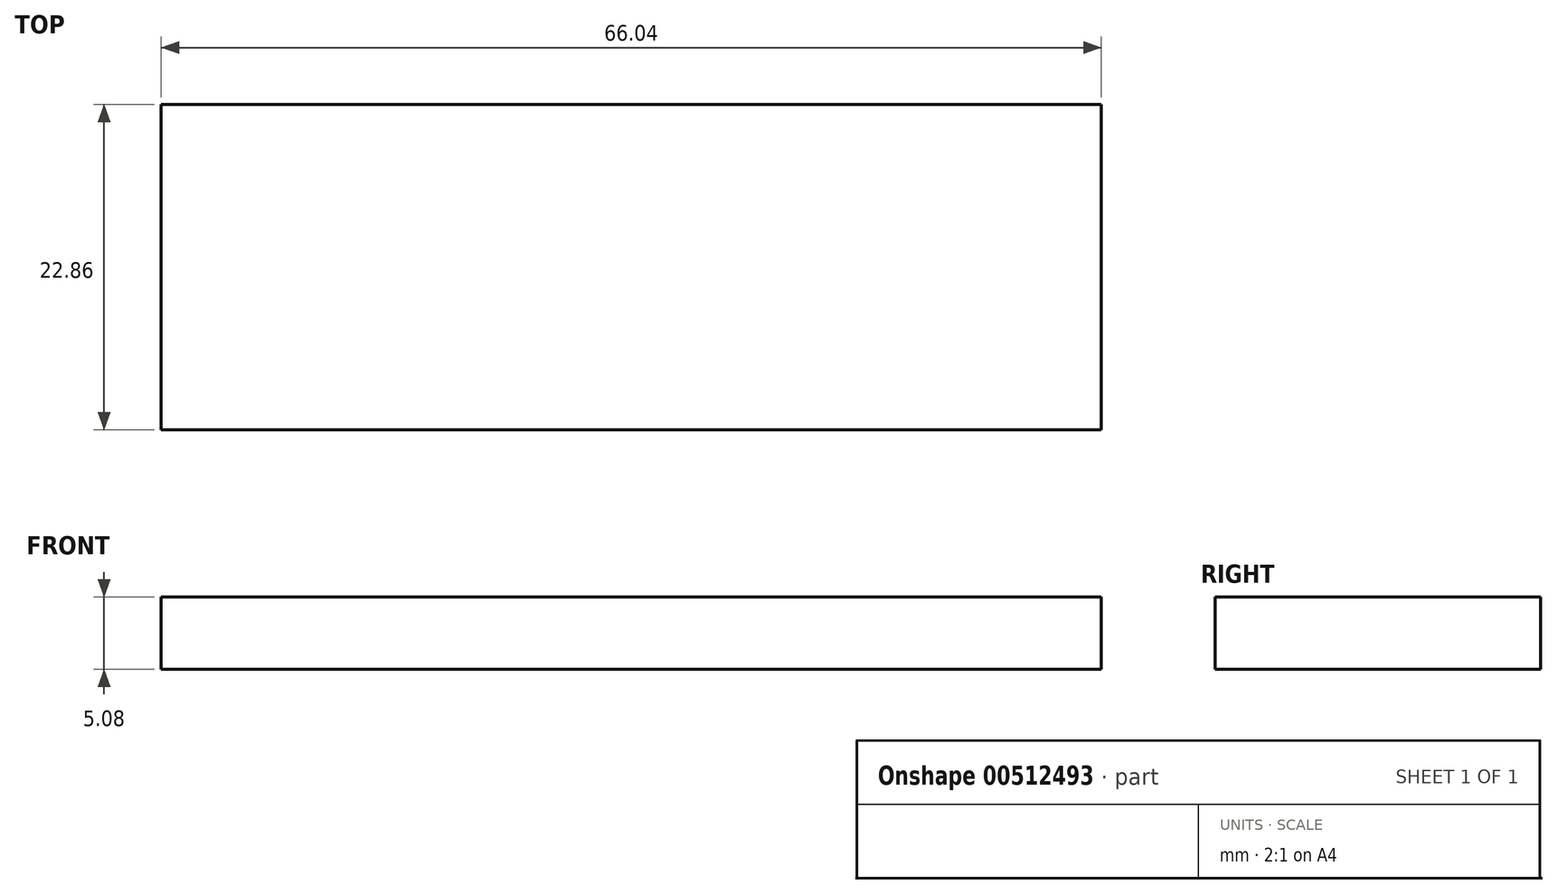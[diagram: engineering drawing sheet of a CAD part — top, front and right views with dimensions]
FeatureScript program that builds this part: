
annotation { "Feature Type Name" : "Feature", "Feature Type Description" : "" }
export const myFeature = defineFeature(function(context is Context, id is Id, definition is map)
    precondition{}
    {
        {
            var Q0;
            Q0=qCreatedBy(makeId("Top.planeOp"),FACE);
            var sketch = newSketch(context, id + "F0", { "sketchPlane" : qUnion([Q0])});
            skLineSegment(sketch, "E0.bottom", {"start": v(-80, 30.94) * mm, "end": v(-13.97, 30.94) * mm});
            skLineSegment(sketch, "E0.top", {"start": v(-80, 8.08) * mm, "end": v(-13.97, 8.08) * mm});
            skLineSegment(sketch, "E0.left", {"start": v(-80, 30.94) * mm, "end": v(-80, 8.08) * mm});
            skLineSegment(sketch, "E0.right", {"start": v(-13.97, 30.94) * mm, "end": v(-13.97, 8.08) * mm});
            skSolve(sketch);
        }
        {
            var Q0;
            Q0=makeQuery(id+"F0.imprint","IMPRINT",FACE,{"disambiguationData":[TD([[makeQuery(id+"F0.imprint","IMPRINT",EDGE,{"derivedFrom":sQuery(id+"F0.wireOp",EDGE,"E0.bottom")}),-1.0]])]});
            extrude(context, id + "F1", {"entities" : qUnion([Q0]), "depth" : 5.08 * mm});
        }
    });
